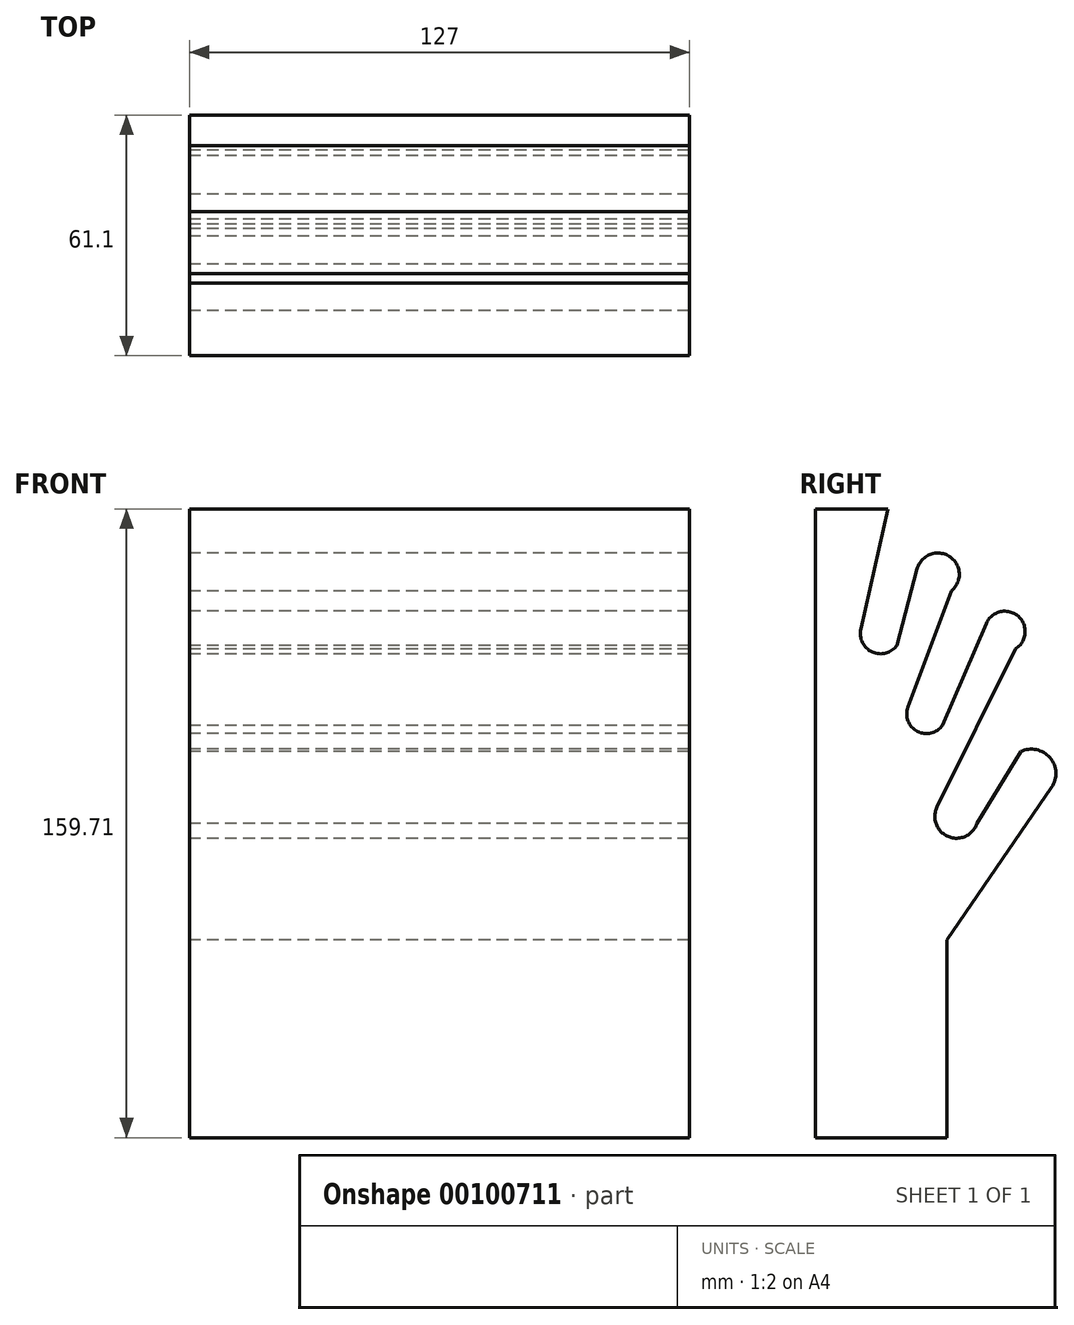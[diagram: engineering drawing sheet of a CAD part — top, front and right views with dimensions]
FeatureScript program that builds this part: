
annotation { "Feature Type Name" : "Feature", "Feature Type Description" : "" }
export const myFeature = defineFeature(function(context is Context, id is Id, definition is map)
    precondition{}
    {
        {
            var Q0;
            Q0=qCreatedBy(makeId("Right.planeOp"),FACE);
            var sketch = newSketch(context, id + "F0", { "sketchPlane" : qUnion([Q0])});
            skLineSegment(sketch, "E0", {"start": v(-67.4, 61.62) * mm, "end": v(-67.4, -98.09) * mm});
            skLineSegment(sketch, "E1", {"start": v(-67.4, 61.62) * mm, "end": v(-48.93, 61.62) * mm});
            skLineSegment(sketch, "E2", {"start": v(-48.93, 61.62) * mm, "end": v(-55.85, 31.16) * mm});
            skPoint(sketch, "E3", {"position": v(-46.62, 27) * mm});
            skArc(sketch, "E4", {"start": v(-55.85, 31.16) * mm, "mid": v(-52.94, 25.3) * mm, "end": v(-46.62, 27) * mm});
            skLineSegment(sketch, "E5", {"start": v(-46.62, 27) * mm, "end": v(-41.54, 46.4) * mm});
            skPoint(sketch, "E5.endSnap0", {"position": v(-52.4, 46.4) * mm});
            skPoint(sketch, "E6", {"position": v(-32.77, 40.85) * mm});
            skArc(sketch, "E7", {"start": v(-32.77, 40.85) * mm, "mid": v(-33.37, 49.61) * mm, "end": v(-41.54, 46.4) * mm});
            skLineSegment(sketch, "E8", {"start": v(-32.77, 40.85) * mm, "end": v(-43.85, 11.3) * mm});
            skPoint(sketch, "E9", {"position": v(-35.08, 6.7) * mm});
            skArc(sketch, "E10", {"start": v(-43.85, 11.3) * mm, "mid": v(-41.5, 5.14) * mm, "end": v(-35.08, 6.7) * mm});
            skLineSegment(sketch, "E11", {"start": v(-35.08, 6.7) * mm, "end": v(-24, 32.54) * mm});
            skPoint(sketch, "E12", {"position": v(-16.62, 26.08) * mm});
            skArc(sketch, "E13", {"start": v(-16.62, 26.08) * mm, "mid": v(-15.86, 34.4) * mm, "end": v(-24, 32.54) * mm});
            skLineSegment(sketch, "E14", {"start": v(-16.62, 26.08) * mm, "end": v(-36.47, -14.08) * mm});
            skPoint(sketch, "E15", {"position": v(-26.31, -18.23) * mm});
            skArc(sketch, "E16", {"start": v(-36.47, -14.08) * mm, "mid": v(-33.62, -21.6) * mm, "end": v(-26.31, -18.23) * mm});
            skLineSegment(sketch, "E17", {"start": v(-26.31, -18.23) * mm, "end": v(-15.23, 0) * mm});
            skPoint(sketch, "E18", {"position": v(-7.39, -9.12) * mm});
            skPoint(sketch, "E18.positionSnap0", {"position": v(-20.77, -9.12) * mm});
            skArc(sketch, "E19", {"start": v(-7.39, -9.12) * mm, "mid": v(-7.8, -1.54) * mm, "end": v(-15.23, 0) * mm});
            skLineSegment(sketch, "E20", {"start": v(-7.39, -9.12) * mm, "end": v(-33.93, -47.81) * mm});
            skLineSegment(sketch, "E21", {"start": v(-33.93, -47.81) * mm, "end": v(-33.93, -98.09) * mm});
            skLineSegment(sketch, "E22", {"start": v(-33.93, -98.09) * mm, "end": v(-67.4, -98.09) * mm});
            skSolve(sketch);
        }
        {
            var Q0;
            Q0=makeQuery(id+"F0.imprint","IMPRINT",FACE,{"disambiguationData":[TD([[makeQuery(id+"F0.imprint","IMPRINT",EDGE,{"derivedFrom":sQuery(id+"F0.wireOp",EDGE,"E0")}),1.0]])]});
            extrude(context, id + "F1", {"entities" : qUnion([Q0]), "depth" : 127 * mm});
        }
    });
